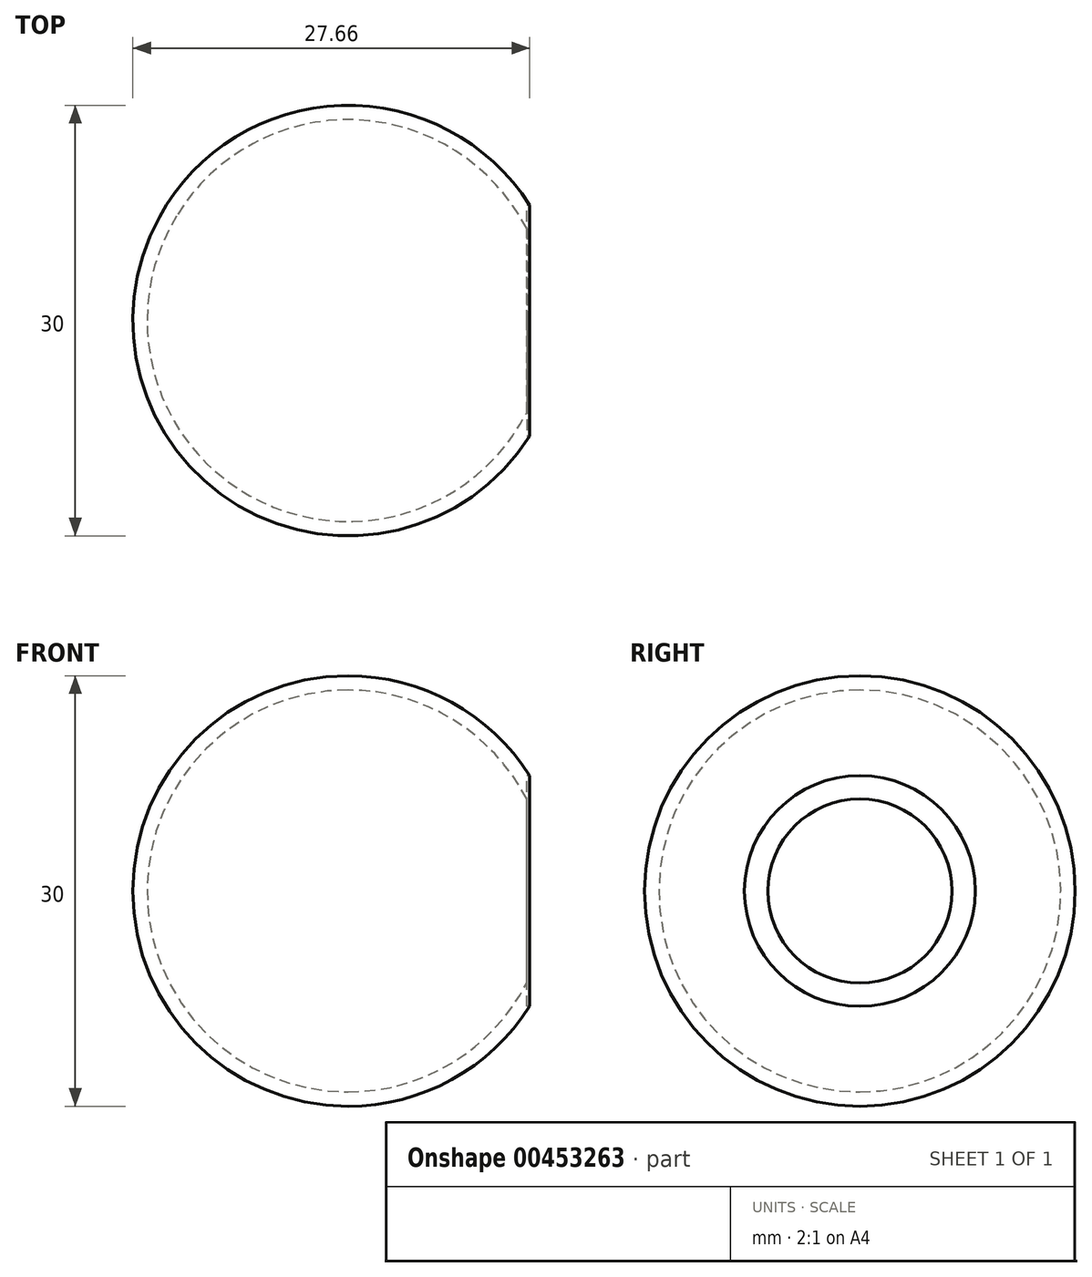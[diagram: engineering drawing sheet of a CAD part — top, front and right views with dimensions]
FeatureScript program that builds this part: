
annotation { "Feature Type Name" : "Feature", "Feature Type Description" : "" }
export const myFeature = defineFeature(function(context is Context, id is Id, definition is map)
    precondition{}
    {
        {
            var Q0;
            Q0=qCreatedBy(makeId("Right.planeOp"),FACE);
            var sketch = newSketch(context, id + "F0", { "sketchPlane" : qUnion([Q0])});
            skCircle(sketch, "E0", {"center": v(0, 0) * mm, "radius": 15 * mm});
            skLineSegment(sketch, "E1", {"start": v(0, 15) * mm, "end": v(0, -15) * mm});
            skSolve(sketch);
        }
        {
            var Q0;
            {var subQ0=sQuery(id+"F0.wireOp",EDGE,"E1");Q0=makeQuery(id+"F0.imprint","IMPRINT",FACE,{"disambiguationData":[TD([[makeQuery(id+"F0.imprint","IMPRINT",EDGE,{"derivedFrom":subQ0}),1.0]])]});}
            var Q1;
            Q1=sQuery(id+"F0.wireOp",EDGE,"E1");
            revolve(context, id + "F1", {"entities" : qUnion([Q0]), "axis" : qUnion([Q1]), "revolveType" : RevolveType.FULL});
        }
        {
            var Q0;
            Q0=qCreatedBy(makeId("Right.planeOp"),FACE);
            cPlane(context, id + "F2", {"entities" : qUnion([Q0]), "cplaneType" : CPlaneType.OFFSET, "offset" : 12.45 * mm, "width" : 152.4 * mm, "height" : 152.4 * mm});
        }
        {
            var Q0;
            Q0=qCreatedBy(id+"F2.planeOp",FACE);
            var sketch = newSketch(context, id + "F3", { "sketchPlane" : qUnion([Q0])});
            skCircle(sketch, "E2", {"center": v(0, 0) * mm, "radius": 8.04 * mm});
            skSolve(sketch);
        }
        {
            var Q0;
            Q0=makeQuery(id+"F1.opRevolve","SWEPT_FACE",FACE,{"disambiguationData":[OSD([sQuery(id+"F0.wireOp",EDGE,"E0")])]});
            var Q1;
            Q1=makeQuery(id+"F1.opRevolve","SWEPT_BODY",BODY,{"disambiguationData":[OSD([sQuery(id+"F0.wireOp",EDGE,"E0"),sQuery(id+"F0.wireOp",EDGE,"E1")])]});
            shell(context, id + "F4", {"isHollow" : true, "entities" : qUnion([Q0]), "parts" : qUnion([Q1]), "thickness" : 1 * mm});
        }
        {
            var Q0;
            Q0 = qSketchRegion(id + "F3", true);
            extrude(context, id + "F5", {"entities" : qUnion([Q0]), "operationType" : NewBodyOperationType.REMOVE, "depth" : 25.4 * mm, "offsetDistance" : 25.4 * mm});
        }
    });
